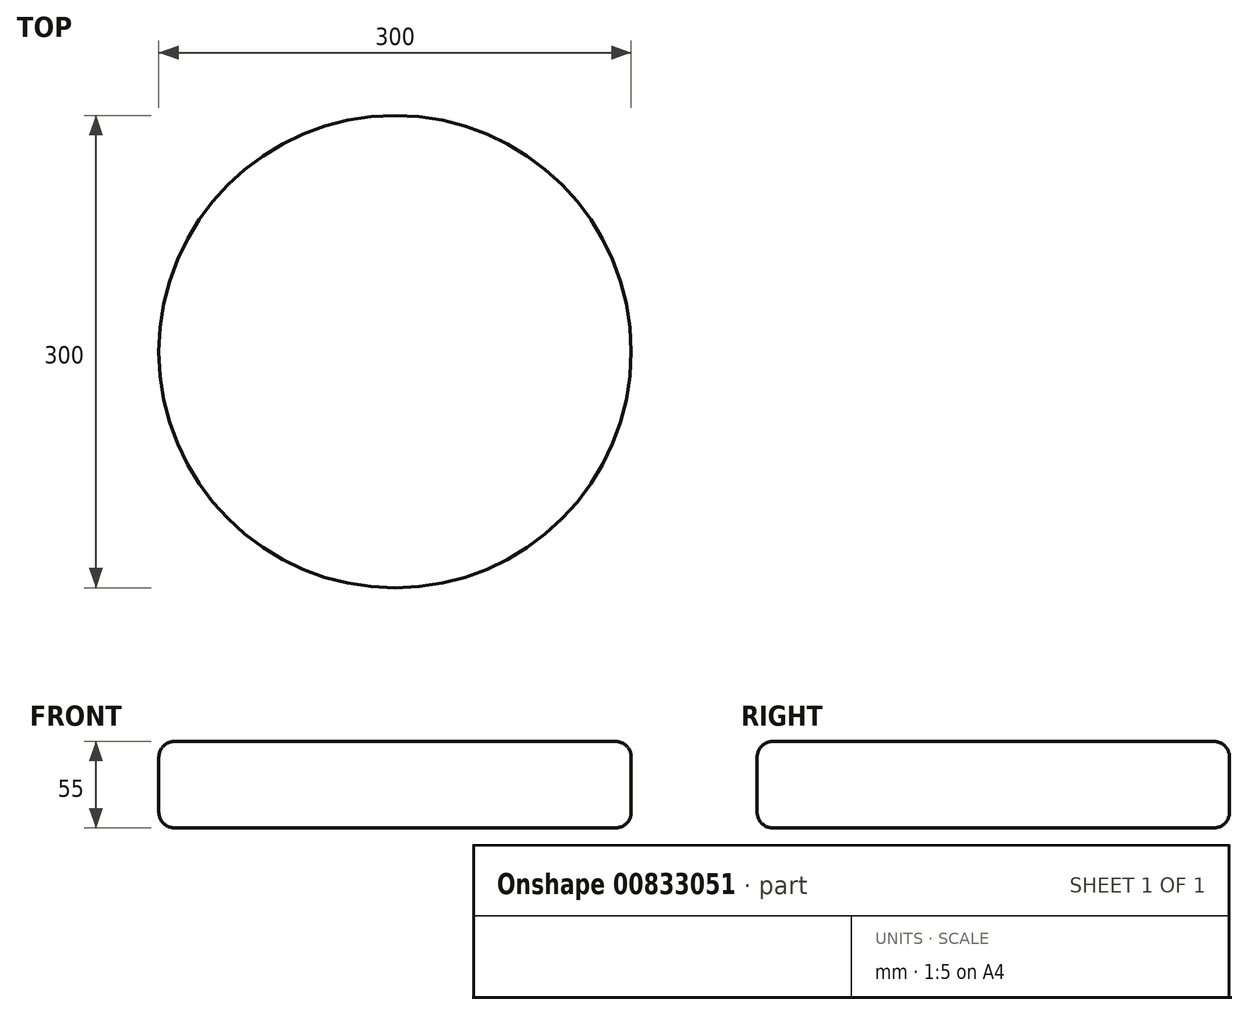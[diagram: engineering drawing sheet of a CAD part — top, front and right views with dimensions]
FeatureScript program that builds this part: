
annotation { "Feature Type Name" : "Feature", "Feature Type Description" : "" }
export const myFeature = defineFeature(function(context is Context, id is Id, definition is map)
    precondition{}
    {
        {
            var Q0;
            Q0=qCreatedBy(makeId("Front.planeOp"),FACE);
            var sketch = newSketch(context, id + "F0", { "sketchPlane" : qUnion([Q0])});
            skLineSegment(sketch, "E0.bottom", {"start": v(0, 0) * mm, "end": v(-150, 0) * mm});
            skLineSegment(sketch, "E0.top", {"start": v(0, 55) * mm, "end": v(-150, 55) * mm});
            skLineSegment(sketch, "E0.left", {"start": v(0, 0) * mm, "end": v(0, 55) * mm});
            skLineSegment(sketch, "E0.right", {"start": v(-150, 0) * mm, "end": v(-150, 55) * mm});
            skSolve(sketch);
        }
        {
            var Q0;
            Q0=makeQuery(id+"F0.imprint","IMPRINT",FACE,{"disambiguationData":[TD([[makeQuery(id+"F0.imprint","IMPRINT",EDGE,{"derivedFrom":sQuery(id+"F0.wireOp",EDGE,"E0.bottom")}),-1.0]])]});
            var Q1;
            Q1=sQuery(id+"F0.wireOp",EDGE,"E0.left");
            revolve(context, id + "F1", {"surfaceOperationType" : NewSurfaceOperationType.NEW, "entities" : qUnion([Q0]), "axis" : qUnion([Q1]), "revolveType" : RevolveType.FULL});
        }
        {
            var Q0;
            Q0=makeQuery(id+"F1.opRevolve","SWEPT_EDGE",EDGE,{"disambiguationData":[OSD([sQuery(id+"F0.wireOp",EDGE,"E0.top"),sQuery(id+"F0.wireOp",EDGE,"E0.right")])]});
            var Q1;
            Q1=makeQuery(id+"F1.opRevolve","SWEPT_EDGE",EDGE,{"disambiguationData":[OSD([sQuery(id+"F0.wireOp",EDGE,"E0.bottom"),sQuery(id+"F0.wireOp",EDGE,"E0.right")])]});
            fillet(context, id + "F2", {"entities" : qUnion([Q0, Q1]), "radius" : 10 * mm, "tangentPropagation" : true, "allowEdgeOverflow" : false});
        }
    });
